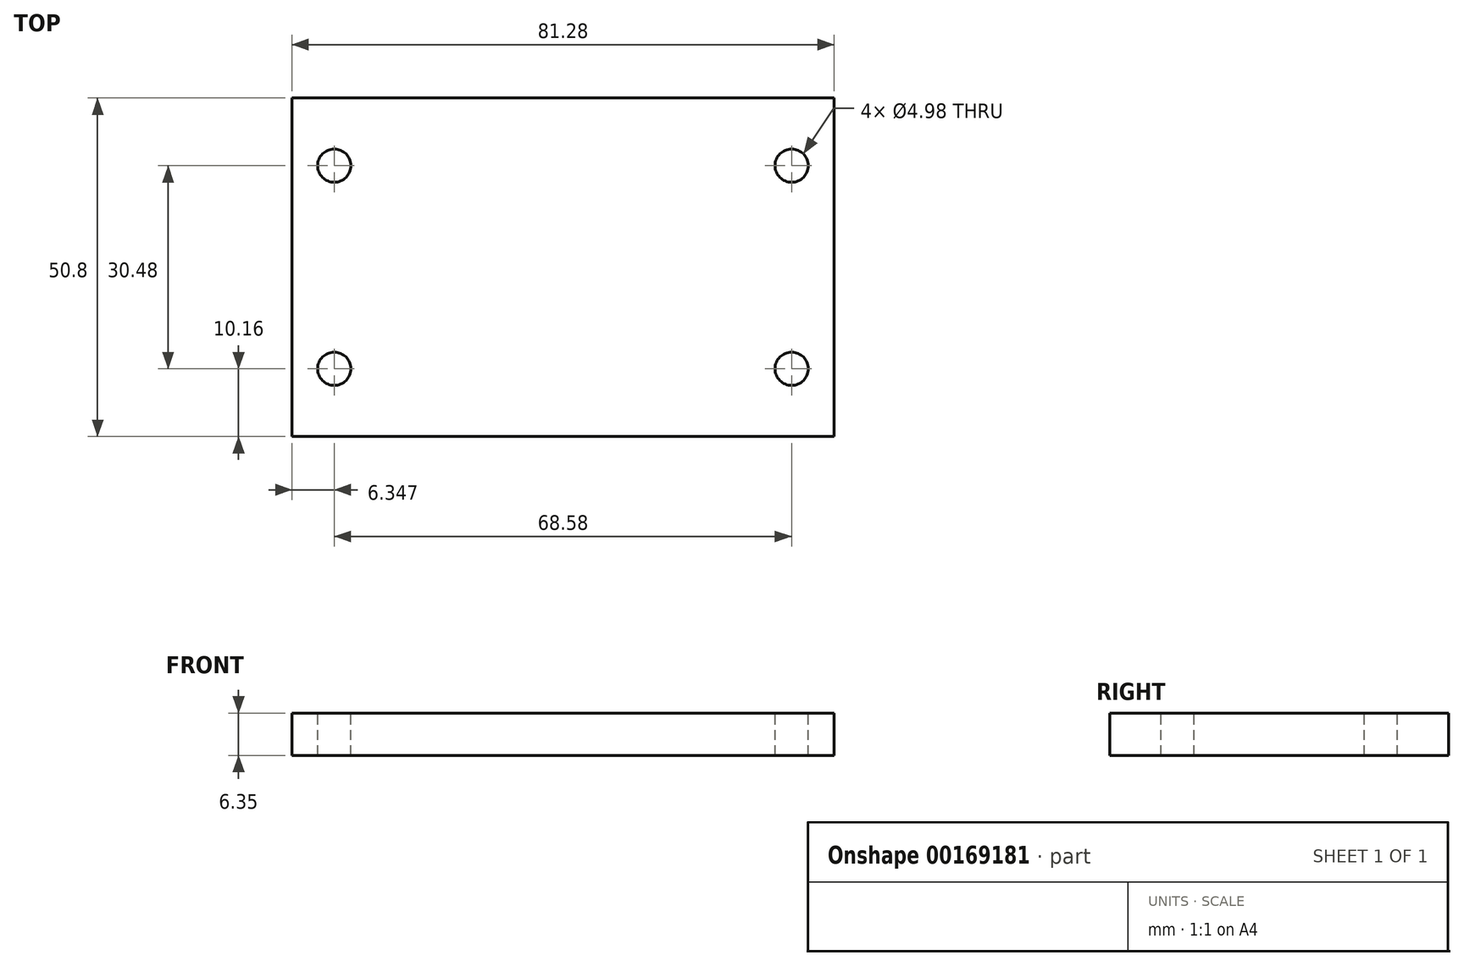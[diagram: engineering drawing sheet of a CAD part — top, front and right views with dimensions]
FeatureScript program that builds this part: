
annotation { "Feature Type Name" : "Feature", "Feature Type Description" : "" }
export const myFeature = defineFeature(function(context is Context, id is Id, definition is map)
    precondition{}
    {
        {
            var Q0;
            Q0=qCreatedBy(makeId("Top.planeOp"),FACE);
            var sketch = newSketch(context, id + "F0", { "sketchPlane" : qUnion([Q0])});
            skLineSegment(sketch, "E0.bottom", {"start": v(-147, -25.4) * mm, "end": v(-65.72, -25.4) * mm});
            skLineSegment(sketch, "E0.top", {"start": v(-147, 25.4) * mm, "end": v(-65.72, 25.4) * mm});
            skLineSegment(sketch, "E0.left", {"start": v(-147, -25.4) * mm, "end": v(-147, 25.4) * mm});
            skLineSegment(sketch, "E0.right", {"start": v(-65.72, -25.4) * mm, "end": v(-65.72, 25.4) * mm});
            skPoint(sketch, "E1", {"position": v(-140.65, 15.24) * mm});
            skPoint(sketch, "E2", {"position": v(-140.65, -15.24) * mm});
            skPoint(sketch, "E3", {"position": v(-72.07, 15.24) * mm});
            skPoint(sketch, "E4", {"position": v(-72.07, -15.24) * mm});
            skSolve(sketch);
        }
        {
            var Q0;
            Q0=makeQuery(id+"F0.imprint","IMPRINT",FACE,{"disambiguationData":[TD([[makeQuery(id+"F0.imprint","IMPRINT",EDGE,{"derivedFrom":sQuery(id+"F0.wireOp",EDGE,"E0.bottom")}),1.0]])]});
            extrude(context, id + "F1", {"entities" : qUnion([Q0]), "oppositeDirection" : true, "depth" : 6.35 * mm});
        }
        {
            var Q0;
            Q0=sQuery(id+"F0.wireOp",VERTEX,"E1");
            var Q1;
            Q1=sQuery(id+"F0.wireOp",VERTEX,"E2");
            var Q2;
            Q2=sQuery(id+"F0.wireOp",VERTEX,"E3");
            var Q3;
            Q3=sQuery(id+"F0.wireOp",VERTEX,"E4");
            var Q4;
            Q4=makeQuery(id+"F1.opExtrude","SWEPT_BODY",BODY,{"disambiguationData":[OSD([sQuery(id+"F0.wireOp",EDGE,"E0.bottom"),sQuery(id+"F0.wireOp",EDGE,"E0.top"),sQuery(id+"F0.wireOp",EDGE,"E0.left"),sQuery(id+"F0.wireOp",EDGE,"E0.right")])]});
            hole(context, id + "F2", {"style" : HoleStyle.SIMPLE, "endStyle" : HoleEndStyle.THROUGH, "standardTappedOrClearance" : lookupTablePath({ "standard" : "ANSI", "fit" : "Close", "size" : "#10", "type" : "Clearance" }), "standardBlindInLast" : lookupTablePath({ "fit" : "Close", "standard" : "ANSI", "size" : "#10", "type" : "Clearance" }), "holeDiameter" : 4.98 * mm, "startFromSketch" : true, "locations" : qUnion([Q0, Q1, Q2, Q3]), "scope" : qUnion([Q4]), "isTappedThrough" : true});
        }
    });
